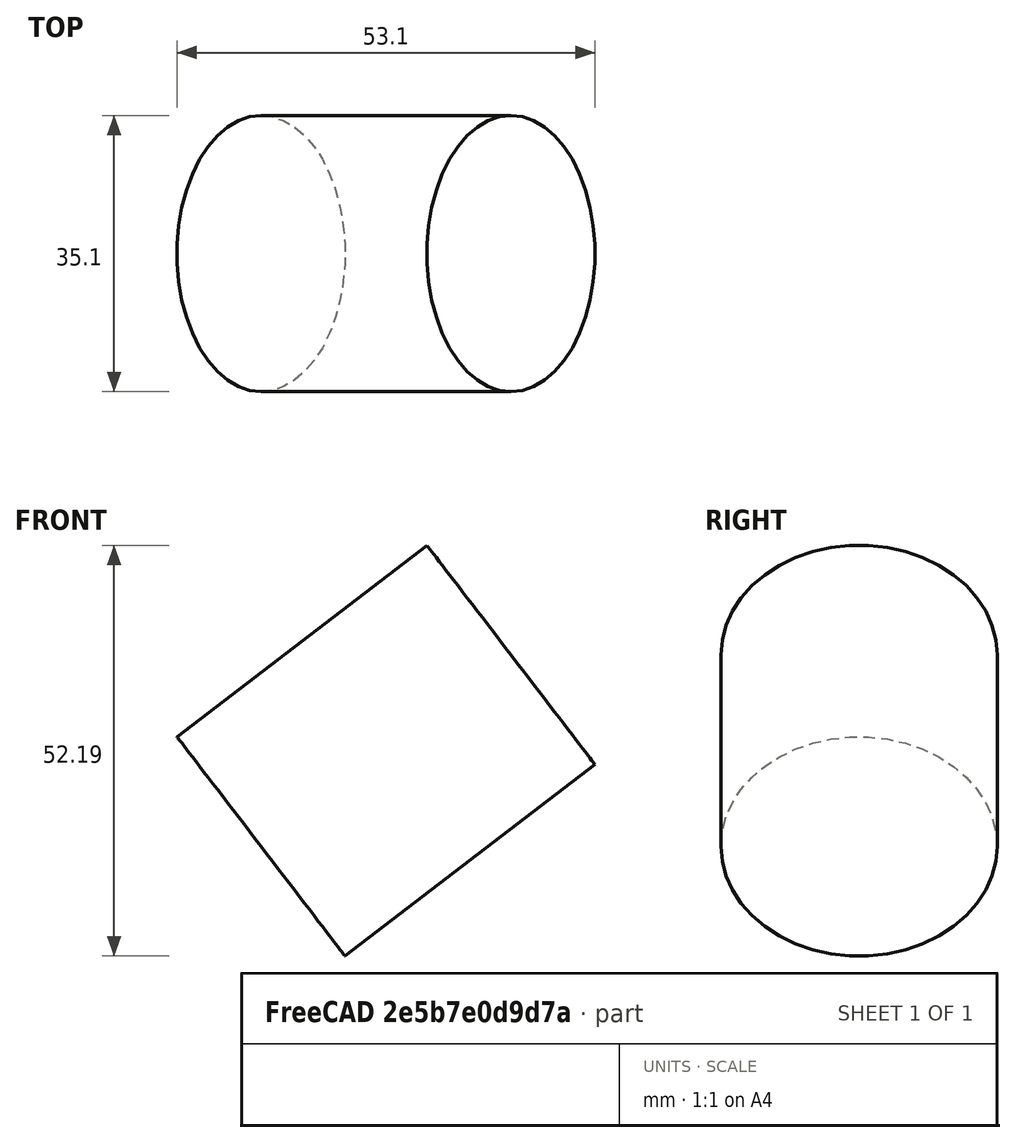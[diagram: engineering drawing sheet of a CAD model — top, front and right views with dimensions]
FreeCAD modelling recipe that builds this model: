
FCSTD DOCUMENT  (FreeCAD 1.0R39319 (Git))
Label: binder
License: All rights reserved
LicenseURL: https://en.wikipedia.org/wiki/All_rights_reserved
objects: Sketcher::SketchObject×3, PartDesign::Plane×1, PartDesign::Pad×1, PartDesign::SubShapeBinder×1, PartDesign::Body×1
note: 12 computed .brp shape members not serialized (recipe doc carries the construction recipe); baked Part::Feature solids carry a one-line shape summary decoded from their .brp

FEATURE [Sketcher::SketchObject] Sketch
  ArcFitTolerance = 1e-06
  AttachmentSupport = -> [XZ_Plane]
  FullyConstrained = false
  MakeInternals = false
  MapMode = 5
  Placement = pos=(0,0,0) rot=(1,0,0;1.5708rad)
  sketch-geometry (1):
    g0: LineSegment StartX=0 StartY=0 StartZ=0 EndX=49.7392 EndY=38.1359 EndZ=0
  constraints (1):
    c: Coincident(g-1,g0)
FEATURE [PartDesign::Plane] DatumPlane
  AttachmentSupport = -> [Sketch]
  Length = 65.4599
  MapMode = 7
  Placement = pos=(49.7392,8.5e-15,38.1359) rot=(0.667642,-0.667642,-0.329404;2.50517rad)
  ResizeMode = 0
  Width = 134.964
FEATURE [Sketcher::SketchObject] Sketch001
  ArcFitTolerance = 1e-06
  AttachmentSupport = -> [DatumPlane]
  FullyConstrained = false
  MakeInternals = false
  MapMode = 5
  Placement = pos=(49.7392,8.5e-15,38.1359) rot=(0.667642,-0.667642,-0.329404;2.50517rad)
  sketch-geometry (1):
    g0: Circle CenterX=0 CenterY=0 CenterZ=0 NormalX=0 NormalY=0 NormalZ=1 AngleXU=0 Radius=17.5465
  constraints (1):
    c: Coincident(g0,g-1)
FEATURE [PartDesign::Pad] Pad
  Direction = (-0.793587,-1e-16,-0.608457)
  Length = 40
  Length2 = 10
  Placement = pos=(49.7392,8.5e-15,38.1359) rot=(0.667642,-0.667642,-0.329404;2.50517rad)
  Profile = -> Sketch001
  ReferenceAxis = -> Sketch001 [N_Axis]
  Refine = true
  Suppressed = false
  Type = 0
FEATURE [PartDesign::SubShapeBinder] Binder
  BindCopyOnChange = 0
  BindMode = 0
  ClaimChildren = false
  Context = -> Body [Binder.]
  Fuse = false
  MakeFace = true
  OffsetFill = false
  OffsetIntersection = false
  OffsetJoinType = 0
  OffsetOpenResult = false
  PartialLoad = false
  Placement = pos=(0,0,5) rot=(0,0,1;0rad)
  Refine = true
  Relative = true
  Support = -> [Pad[Face2]]
  _Version = 2
FEATURE [Sketcher::SketchObject] Sketch002
  ArcFitTolerance = 1e-06
  AttachmentOffset = pos=(0,0,5) rot=(0,0,1;0rad)
  AttachmentSupport = -> [Pad]
  FullyConstrained = false
  MakeInternals = false
  MapMode = 5
  Placement = pos=(53.7071,7.9e-15,41.1782) rot=(-0.404623,0.404623,-0.820098;1.76784rad)
  sketch-geometry (1):
    g0: Circle CenterX=0 CenterY=0 CenterZ=0 NormalX=0 NormalY=0 NormalZ=1 AngleXU=0 Radius=17.5346
  constraints (1):
    c: Coincident(g0,g-1)
FEATURE [PartDesign::Body] Body
  AllowCompound = false
  Group = -> [Sketch,DatumPlane,Sketch001,Pad,Binder,Sketch002]
  Origin = -> Origin
  Tip = -> Pad
